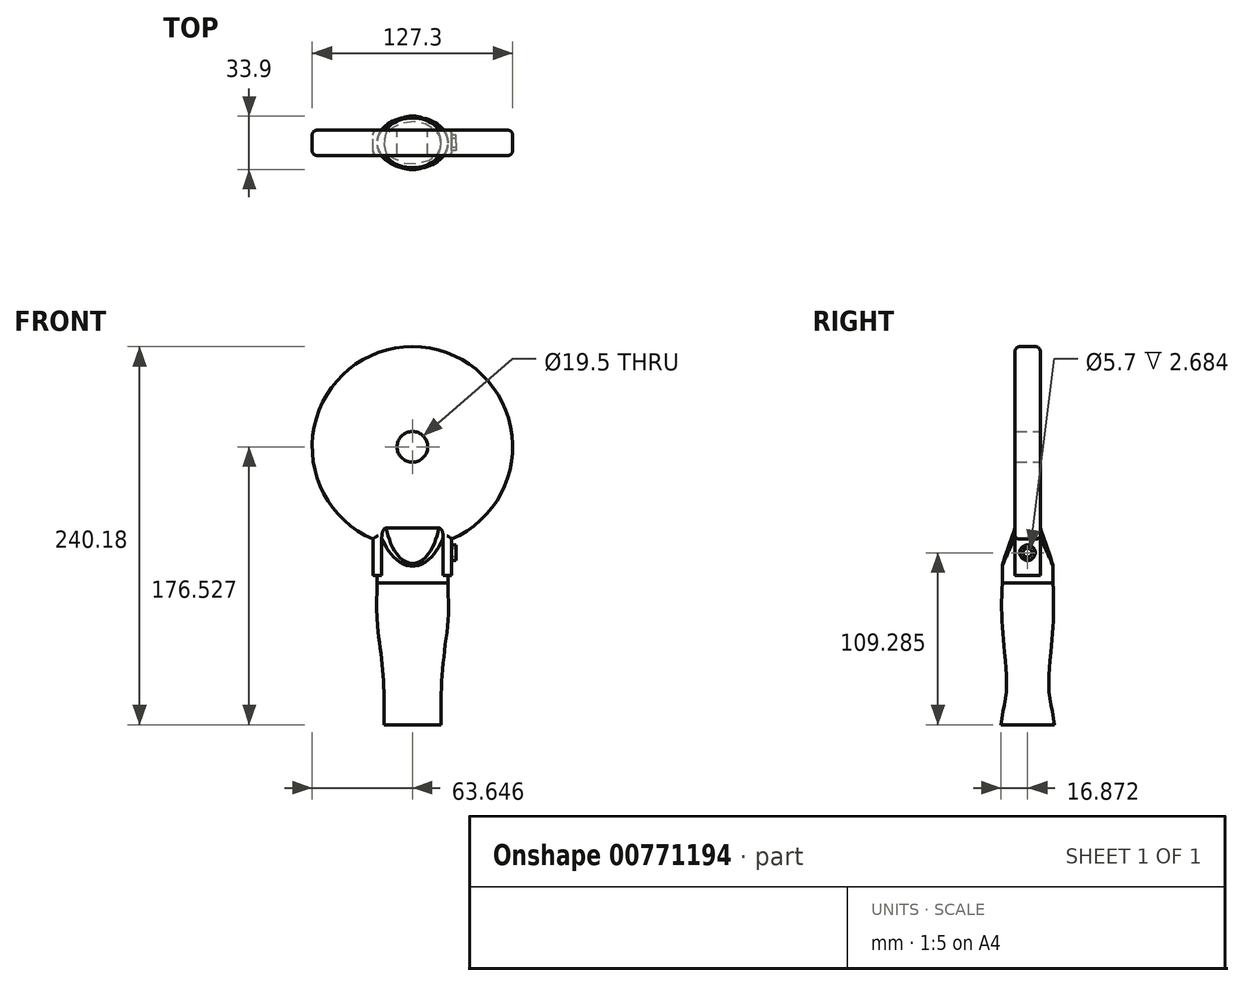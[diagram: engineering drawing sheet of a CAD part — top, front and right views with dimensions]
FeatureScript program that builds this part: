
annotation { "Feature Type Name" : "Feature", "Feature Type Description" : "" }
export const myFeature = defineFeature(function(context is Context, id is Id, definition is map)
    precondition{}
    {
        {
            var Q0;
            Q0=qCreatedBy(makeId("Front.planeOp"),FACE);
            var sketch = newSketch(context, id + "F0", { "sketchPlane" : qUnion([Q0])});
            skLineSegment(sketch, "E0", {"start": v(0, 0) * mm, "end": v(0, 140.42) * mm, "construction": true});
            skSolve(sketch);
        }
        {
            var Q0;
            Q0=qCreatedBy(makeId("Top.planeOp"),FACE);
            var sketch = newSketch(context, id + "F1", { "sketchPlane" : qUnion([Q0])});
            skEllipse(sketch, "E1", {"center": v(0, 0) * mm, "majorRadius": 18.1 * mm, "minorRadius": 16.95 * mm, "majorAxis": v(1, 0)});
            skSolve(sketch);
        }
        {
            var Q0;
            Q0=qCreatedBy(makeId("Top.planeOp"),FACE);
            cPlane(context, id + "F2", {"entities" : qUnion([Q0]), "cplaneType" : CPlaneType.OFFSET, "offset" : 10 * mm, "width" : 150 * mm, "height" : 150 * mm});
        }
        {
            var Q0;
            Q0=qCreatedBy(id+"F2.planeOp",FACE);
            var sketch = newSketch(context, id + "F3", { "sketchPlane" : qUnion([Q0])});
            skEllipse(sketch, "E2", {"center": v(0, 0) * mm, "majorRadius": 18.05 * mm, "minorRadius": 15.3 * mm, "majorAxis": v(1, 0)});
            skSolve(sketch);
        }
        {
            var Q0;
            Q0=qCreatedBy(id+"F2.planeOp",FACE);
            cPlane(context, id + "F4", {"entities" : qUnion([Q0]), "cplaneType" : CPlaneType.OFFSET, "offset" : 10 * mm, "width" : 150 * mm, "height" : 150 * mm});
        }
        {
            var Q0;
            Q0=qCreatedBy(id+"F4.planeOp",FACE);
            var sketch = newSketch(context, id + "F5", { "sketchPlane" : qUnion([Q0])});
            skEllipse(sketch, "E3", {"center": v(0, 0) * mm, "majorRadius": 18.2 * mm, "minorRadius": 13.6 * mm, "majorAxis": v(1, 0)});
            skSolve(sketch);
        }
        {
            var Q0;
            Q0=qCreatedBy(id+"F4.planeOp",FACE);
            cPlane(context, id + "F6", {"entities" : qUnion([Q0]), "cplaneType" : CPlaneType.OFFSET, "offset" : 10 * mm, "width" : 150 * mm, "height" : 150 * mm});
        }
        {
            var Q0;
            Q0=qCreatedBy(id+"F6.planeOp",FACE);
            var sketch = newSketch(context, id + "F7", { "sketchPlane" : qUnion([Q0])});
            skEllipse(sketch, "E4", {"center": v(0, 0) * mm, "majorRadius": 18.55 * mm, "minorRadius": 13.55 * mm, "majorAxis": v(1, 0)});
            skSolve(sketch);
        }
        {
            var Q0;
            Q0=qCreatedBy(id+"F6.planeOp",FACE);
            cPlane(context, id + "F8", {"entities" : qUnion([Q0]), "cplaneType" : CPlaneType.OFFSET, "offset" : 10 * mm, "width" : 150 * mm, "height" : 150 * mm});
        }
        {
            var Q0;
            Q0=qCreatedBy(id+"F8.planeOp",FACE);
            var sketch = newSketch(context, id + "F9", { "sketchPlane" : qUnion([Q0])});
            skEllipse(sketch, "E5", {"center": v(0, 0) * mm, "majorRadius": 19.5 * mm, "minorRadius": 14.15 * mm, "majorAxis": v(1, 0)});
            skSolve(sketch);
        }
        {
            var Q0;
            Q0=qCreatedBy(id+"F8.planeOp",FACE);
            cPlane(context, id + "F10", {"entities" : qUnion([Q0]), "cplaneType" : CPlaneType.OFFSET, "offset" : 10 * mm, "width" : 150 * mm, "height" : 150 * mm});
        }
        {
            var Q0;
            Q0=qCreatedBy(id+"F10.planeOp",FACE);
            var sketch = newSketch(context, id + "F11", { "sketchPlane" : qUnion([Q0])});
            skEllipse(sketch, "E6", {"center": v(0, 0) * mm, "majorRadius": 20.7 * mm, "minorRadius": 15.05 * mm, "majorAxis": v(1, 0)});
            skSolve(sketch);
        }
        {
            var Q0;
            Q0=qCreatedBy(id+"F10.planeOp",FACE);
            cPlane(context, id + "F12", {"entities" : qUnion([Q0]), "cplaneType" : CPlaneType.OFFSET, "offset" : 10 * mm, "width" : 150 * mm, "height" : 150 * mm});
        }
        {
            var Q0;
            Q0=qCreatedBy(id+"F12.planeOp",FACE);
            var sketch = newSketch(context, id + "F13", { "sketchPlane" : qUnion([Q0])});
            skEllipse(sketch, "E7", {"center": v(0, 0) * mm, "majorRadius": 22 * mm, "minorRadius": 15.9 * mm, "majorAxis": v(1, 0)});
            skSolve(sketch);
        }
        {
            var Q0;
            Q0=qCreatedBy(id+"F12.planeOp",FACE);
            cPlane(context, id + "F14", {"entities" : qUnion([Q0]), "cplaneType" : CPlaneType.OFFSET, "offset" : 10 * mm, "width" : 150 * mm, "height" : 150 * mm});
        }
        {
            var Q0;
            Q0=qCreatedBy(id+"F14.planeOp",FACE);
            var sketch = newSketch(context, id + "F15", { "sketchPlane" : qUnion([Q0])});
            skEllipse(sketch, "E8", {"center": v(0, 0) * mm, "majorRadius": 22.7 * mm, "minorRadius": 16.4 * mm, "majorAxis": v(1, 0)});
            skSolve(sketch);
        }
        {
            var Q0;
            Q0=qCreatedBy(id+"F14.planeOp",FACE);
            cPlane(context, id + "F16", {"entities" : qUnion([Q0]), "cplaneType" : CPlaneType.OFFSET, "offset" : 10 * mm, "width" : 150 * mm, "height" : 150 * mm});
        }
        {
            var Q0;
            Q0=qCreatedBy(id+"F16.planeOp",FACE);
            var sketch = newSketch(context, id + "F17", { "sketchPlane" : qUnion([Q0])});
            skEllipse(sketch, "E9", {"center": v(0, 0) * mm, "majorRadius": 22.7 * mm, "minorRadius": 16.5 * mm, "majorAxis": v(1, 0)});
            skSolve(sketch);
        }
        {
            var Q0;
            Q0=qCreatedBy(id+"F16.planeOp",FACE);
            cPlane(context, id + "F18", {"entities" : qUnion([Q0]), "cplaneType" : CPlaneType.OFFSET, "offset" : 10 * mm, "width" : 150 * mm, "height" : 150 * mm});
        }
        {
            var Q0;
            Q0=qCreatedBy(id+"F18.planeOp",FACE);
            var sketch = newSketch(context, id + "F19", { "sketchPlane" : qUnion([Q0])});
            skEllipse(sketch, "E10", {"center": v(0, 0) * mm, "majorRadius": 22.5 * mm, "minorRadius": 16.1 * mm, "majorAxis": v(1, 0)});
            skSolve(sketch);
        }
        {
            var Q0;
            Q0=makeQuery(id+"F1.imprint","IMPRINT",FACE,{"disambiguationData":[TD([[makeQuery(id+"F1.imprint","IMPRINT",EDGE,{"derivedFrom":sQuery(id+"F1.wireOp",EDGE,"E1")}),1.0]])]});
            var Q1;
            Q1=makeQuery(id+"F3.imprint","IMPRINT",FACE,{"disambiguationData":[TD([[makeQuery(id+"F3.imprint","IMPRINT",EDGE,{"derivedFrom":sQuery(id+"F3.wireOp",EDGE,"E2")}),1.0]])]});
            var Q2;
            Q2=makeQuery(id+"F5.imprint","IMPRINT",FACE,{"disambiguationData":[TD([[makeQuery(id+"F5.imprint","IMPRINT",EDGE,{"derivedFrom":sQuery(id+"F5.wireOp",EDGE,"E3")}),1.0]])]});
            var Q3;
            Q3=makeQuery(id+"F7.imprint","IMPRINT",FACE,{"disambiguationData":[TD([[makeQuery(id+"F7.imprint","IMPRINT",EDGE,{"derivedFrom":sQuery(id+"F7.wireOp",EDGE,"E4")}),1.0]])]});
            var Q4;
            Q4=makeQuery(id+"F9.imprint","IMPRINT",FACE,{"disambiguationData":[TD([[makeQuery(id+"F9.imprint","IMPRINT",EDGE,{"derivedFrom":sQuery(id+"F9.wireOp",EDGE,"E5")}),1.0]])]});
            var Q5;
            Q5=makeQuery(id+"F11.imprint","IMPRINT",FACE,{"disambiguationData":[TD([[makeQuery(id+"F11.imprint","IMPRINT",EDGE,{"derivedFrom":sQuery(id+"F11.wireOp",EDGE,"E6")}),1.0]])]});
            var Q6;
            Q6=makeQuery(id+"F13.imprint","IMPRINT",FACE,{"disambiguationData":[TD([[makeQuery(id+"F13.imprint","IMPRINT",EDGE,{"derivedFrom":sQuery(id+"F13.wireOp",EDGE,"E7")}),1.0]])]});
            var Q7;
            Q7=makeQuery(id+"F15.imprint","IMPRINT",FACE,{"disambiguationData":[TD([[makeQuery(id+"F15.imprint","IMPRINT",EDGE,{"derivedFrom":sQuery(id+"F15.wireOp",EDGE,"E8")}),1.0]])]});
            var Q8;
            Q8=makeQuery(id+"F17.imprint","IMPRINT",FACE,{"disambiguationData":[TD([[makeQuery(id+"F17.imprint","IMPRINT",EDGE,{"derivedFrom":sQuery(id+"F17.wireOp",EDGE,"E9")}),1.0]])]});
            var Q9;
            Q9=makeQuery(id+"F19.imprint","IMPRINT",FACE,{"disambiguationData":[TD([[makeQuery(id+"F19.imprint","IMPRINT",EDGE,{"derivedFrom":sQuery(id+"F19.wireOp",EDGE,"E10")}),1.0]])]});
            loft(context, id + "F20", {"sheetProfilesArray" : [{ "sheetProfileEntities" : qUnion([Q0]) }, { "sheetProfileEntities" : qUnion([Q1]) }, { "sheetProfileEntities" : qUnion([Q2]) }, { "sheetProfileEntities" : qUnion([Q3]) }, { "sheetProfileEntities" : qUnion([Q4]) }, { "sheetProfileEntities" : qUnion([Q5]) }, { "sheetProfileEntities" : qUnion([Q6]) }, { "sheetProfileEntities" : qUnion([Q7]) }, { "sheetProfileEntities" : qUnion([Q8]) }, { "sheetProfileEntities" : qUnion([Q9]) }]});
        }
        {
            var Q0;
            Q0=makeQuery(id+"F20.opLoft","CAP_FACE",FACE,{"disambiguationData":[OSD([makeQuery(id+"F19.imprint","IMPRINT",FACE,{"disambiguationData":[TD([[makeQuery(id+"F19.imprint","IMPRINT",EDGE,{"derivedFrom":sQuery(id+"F19.wireOp",EDGE,"E10")}),1.0]])]})])],"isStart":true});
            extrude(context, id + "F21", {"entities" : qUnion([Q0]), "operationType" : NewBodyOperationType.ADD, "depth" : 35 * mm, "offsetDistance" : 25 * mm});
        }
        {
            var Q0;
            Q0=qCreatedBy(makeId("Front.planeOp"),FACE);
            var sketch = newSketch(context, id + "F22", { "sketchPlane" : qUnion([Q0])});
            skLineSegment(sketch, "E11.top", {"start": v(-0.08, 119.9) * mm, "end": v(24.82, 119.9) * mm});
            skLineSegment(sketch, "E11.left", {"start": v(-0.08, 89.9) * mm, "end": v(-0.08, 119.9) * mm});
            skLineSegment(sketch, "E12.MirrorCS", {"start": v(-0.08, 119.9) * mm, "end": v(-24.98, 119.9) * mm});
            skLineSegment(sketch, "E13", {"start": v(-0.08, 89.38) * mm, "end": v(-0.08, 240.38) * mm, "construction": true});
            skCircle(sketch, "E14", {"center": v(-0.08, 176.53) * mm, "radius": 9.75 * mm});
            skCircle(sketch, "E15", {"center": v(-0.08, 176.53) * mm, "radius": 63.65 * mm});
            skLineSegment(sketch, "E16", {"start": v(-0.08, 119.9) * mm, "end": v(54.23, 119.9) * mm, "construction": true});
            skLineSegment(sketch, "E17", {"start": v(-0.08, 89.9) * mm, "end": v(-0.08, 94.9) * mm});
            skLineSegment(sketch, "E18", {"start": v(-0.08, 94.9) * mm, "end": v(24.82, 94.9) * mm});
            skLineSegment(sketch, "E19.MirrorCS", {"start": v(-0.08, 100.44) * mm, "end": v(-0.08, -50.56) * mm, "construction": true});
            skLineSegment(sketch, "E20", {"start": v(-0.08, 94.9) * mm, "end": v(-24.98, 94.9) * mm});
            skLineSegment(sketch, "E21", {"start": v(-24.98, 94.9) * mm, "end": v(-24.98, 119.9) * mm});
            skLineSegment(sketch, "E22", {"start": v(24.82, 94.9) * mm, "end": v(24.82, 119.9) * mm});
            skSolve(sketch);
        }
        {
            var Q0;
            Q0=qCreatedBy(makeId("Right.planeOp"),FACE);
            var sketch = newSketch(context, id + "F23", { "sketchPlane" : qUnion([Q0])});
            skLineSegment(sketch, "E23", {"start": v(-0.08, 0.28) * mm, "end": v(-0.08, 109.28) * mm});
            skCircle(sketch, "E24", {"center": v(-0.08, 109.28) * mm, "radius": 4.9 * mm});
            skCircle(sketch, "E25", {"center": v(-0.08, 109.28) * mm, "radius": 2.85 * mm});
            skSolve(sketch);
        }
        {
            var Q0;
            Q0 = qSketchRegion(id + "F23", true);
            extrude(context, id + "F24", {"entities" : qUnion([Q0]), "operationType" : NewBodyOperationType.ADD, "depth" : 27.5 * mm, "offsetDistance" : 25 * mm});
        }
        {
            var Q0;
            {var subQ5=sQuery(id+"F22.wireOp",EDGE,"E11.top");Q0=makeQuery(id+"F22.imprint","IMPRINT",FACE,{"disambiguationData":[TD([[makeQuery(id+"F22.imprint","IMPRINT",EDGE,{"derivedFrom":subQ5}),1.0]])]});}
            var Q1;
            {var subQ0=sQuery(id+"F22.wireOp",EDGE,"E11.bottom");Q1=makeQuery(id+"F22.imprint","IMPRINT",FACE,{"disambiguationData":[TD([[makeQuery(id+"F22.imprint","IMPRINT",EDGE,{"derivedFrom":subQ0}),1.0]])]});}
            var Q2;
            {var subQ0=sQuery(id+"F22.wireOp",EDGE,"E11.top");Q2=makeQuery(id+"F22.imprint","IMPRINT",FACE,{"disambiguationData":[TD([[makeQuery(id+"F22.imprint","IMPRINT",EDGE,{"derivedFrom":subQ0}),-1.0]])]});}
            var Q3;
            {var subQ0=sQuery(id+"F22.wireOp",EDGE,"E12.MirrorCS");Q3=makeQuery(id+"F22.imprint","IMPRINT",FACE,{"disambiguationData":[TD([[makeQuery(id+"F22.imprint","IMPRINT",EDGE,{"derivedFrom":subQ0}),1.0]])]});}
            var Q4;
            {var subQ0=sQuery(id+"F22.wireOp",EDGE,"55a6d1cb-0f40-4dd8-971e-41e56460f39b0.MirrorCS");Q4=makeQuery(id+"F22.imprint","IMPRINT",FACE,{"disambiguationData":[TD([[makeQuery(id+"F22.imprint","IMPRINT",EDGE,{"derivedFrom":subQ0}),-1.0]])]});}
            extrude(context, id + "F25", {"entities" : qUnion([Q0, Q1, Q2, Q3, Q4]), "operationType" : NewBodyOperationType.ADD, "endBound" : BoundingType.SYMMETRIC, "depth" : 16 * mm, "offsetDistance" : 25 * mm});
        }
        {
            var Q0;
            {var subQ0=sQuery(id+"F22.wireOp",EDGE,"E18");Q0=makeQuery(id+"F22.imprint","IMPRINT",FACE,{"disambiguationData":[TD([[makeQuery(id+"F22.imprint","IMPRINT",EDGE,{"derivedFrom":subQ0}),1.0]])]});}
            extrude(context, id + "F26", {"entities" : qUnion([Q0]), "operationType" : NewBodyOperationType.ADD, "endBound" : BoundingType.SYMMETRIC, "depth" : 16 * mm, "offsetDistance" : 25 * mm});
        }
        {
            var Q0;
            {var subQ0=sQuery(id+"F22.wireOp",EDGE,"E20");Q0=makeQuery(id+"F22.imprint","IMPRINT",FACE,{"disambiguationData":[TD([[makeQuery(id+"F22.imprint","IMPRINT",EDGE,{"derivedFrom":subQ0}),-1.0]])]});}
            extrude(context, id + "F27", {"entities" : qUnion([Q0]), "operationType" : NewBodyOperationType.ADD, "endBound" : BoundingType.SYMMETRIC, "depth" : 16 * mm, "offsetDistance" : 25 * mm});
        }
        {
            var Q0;
            Q0=qCreatedBy(makeId("Right.planeOp"),FACE);
            var sketch = newSketch(context, id + "F28", { "sketchPlane" : qUnion([Q0])});
            skLineSegment(sketch, "E26", {"start": v(-20.12, 90) * mm, "end": v(-8, 125) * mm});
            skLineSegment(sketch, "E27", {"start": v(-8, 125) * mm, "end": v(-20.74, 137.98) * mm});
            skLineSegment(sketch, "E28", {"start": v(-20.74, 137.98) * mm, "end": v(-20.12, 90) * mm});
            skLineSegment(sketch, "E29.MirrorCS", {"start": v(8, 125) * mm, "end": v(20.74, 137.98) * mm});
            skLineSegment(sketch, "E30.MirrorCS", {"start": v(20.12, 90) * mm, "end": v(8, 125) * mm});
            skLineSegment(sketch, "E31.MirrorCS", {"start": v(20.74, 137.98) * mm, "end": v(20.12, 90) * mm});
            skSolve(sketch);
        }
        {
            var Q0;
            Q0=makeQuery(id+"F28.imprint","IMPRINT",FACE,{"disambiguationData":[TD([[makeQuery(id+"F28.imprint","IMPRINT",EDGE,{"derivedFrom":sQuery(id+"F28.wireOp",EDGE,"E26")}),1.0]])]});
            var Q1;
            Q1=makeQuery(id+"F28.imprint","IMPRINT",FACE,{"disambiguationData":[TD([[makeQuery(id+"F28.imprint","IMPRINT",EDGE,{"derivedFrom":sQuery(id+"F28.wireOp",EDGE,"E29.MirrorCS")}),-1.0]])]});
            extrude(context, id + "F29", {"entities" : qUnion([Q0, Q1]), "operationType" : NewBodyOperationType.REMOVE, "endBound" : BoundingType.SYMMETRIC, "oppositeDirection" : true, "depth" : 70 * mm, "offsetDistance" : 25 * mm});
        }
        {
            var Q0;
            Q0=makeQuery(id+"F25.opExtrude","CAP_EDGE",EDGE,{"disambiguationData":[OSD([sQuery(id+"F22.wireOp",EDGE,"d095e0c7-c276-491f-b3f2-35c4f7110da40.MirrorCS")])],"isStart":true});
            var Q1;
            Q1=makeQuery(id+"F25.opExtrude","CAP_EDGE",EDGE,{"disambiguationData":[OSD([sQuery(id+"F22.wireOp",EDGE,"E15")])],"isStart":true});
            var Q2;
            Q2=makeQuery(id+"F25.opExtrude","CAP_EDGE",EDGE,{"disambiguationData":[OSD([sQuery(id+"F22.wireOp",EDGE,"E15")])],"isStart":false});
            var Q3;
            Q3=makeQuery(id+"F25.opExtrude","CAP_EDGE",EDGE,{"disambiguationData":[OSD([sQuery(id+"F22.wireOp",EDGE,"d095e0c7-c276-491f-b3f2-35c4f7110da40.MirrorCS")])],"isStart":false});
            var Q4;
            Q4=makeQuery(id+"F25.opExtrude","CAP_EDGE",EDGE,{"disambiguationData":[OSD([sQuery(id+"F22.wireOp",EDGE,"E11.right")])],"isStart":true});
            var Q5;
            Q5=makeQuery(id+"F25.opExtrude","CAP_EDGE",EDGE,{"disambiguationData":[OSD([sQuery(id+"F22.wireOp",EDGE,"E11.right")])],"isStart":false});
            fillet(context, id + "F30", {"entities" : qUnion([Q0, Q1, Q2, Q3, Q4, Q5]), "radius" : 3 * mm, "tangentPropagation" : true, "allowEdgeOverflow" : false});
        }
        {
            var Q0;
            {var subQ0=sQuery(id+"F19.wireOp",EDGE,"E10");Q0=makeQuery(id+"F29.boolean.opBoolean","INTERSECT",EDGE,{"derivedFrom":[makeQuery(id+"F25.boolean.opBoolean","SPLIT",FACE,{"disambiguationData":[TD([makeQuery(id+"F25.opExtrude","CAP_FACE",FACE,{"disambiguationData":[OSD([sQuery(id+"F22.wireOp",EDGE,"E11.bottom"),sQuery(id+"F22.wireOp",EDGE,"E11.right"),sQuery(id+"F22.wireOp",EDGE,"d095e0c7-c276-491f-b3f2-35c4f7110da40.MirrorCS"),sQuery(id+"F22.wireOp",EDGE,"55a6d1cb-0f40-4dd8-971e-41e56460f39b0.MirrorCS"),sQuery(id+"F22.wireOp",EDGE,"E14"),sQuery(id+"F22.wireOp",EDGE,"E15")])],"isStart":false})])],"derivedFrom":makeQuery(id+"F21.opExtrude","SWEPT_FACE",FACE,{"disambiguationData":[OSD([subQ0])]})}),makeQuery(id+"F29.opExtrude","SWEPT_FACE",FACE,{"disambiguationData":[OSD([sQuery(id+"F28.wireOp",EDGE,"E26")])]})]});}
            var Q1;
            {var subQ0=sQuery(id+"F19.wireOp",EDGE,"E10");Q1=makeQuery(id+"F29.boolean.opBoolean","INTERSECT",EDGE,{"derivedFrom":[makeQuery(id+"F25.boolean.opBoolean","SPLIT",FACE,{"disambiguationData":[TD([makeQuery(id+"F25.opExtrude","CAP_FACE",FACE,{"disambiguationData":[OSD([sQuery(id+"F22.wireOp",EDGE,"E11.bottom"),sQuery(id+"F22.wireOp",EDGE,"E11.right"),sQuery(id+"F22.wireOp",EDGE,"d095e0c7-c276-491f-b3f2-35c4f7110da40.MirrorCS"),sQuery(id+"F22.wireOp",EDGE,"55a6d1cb-0f40-4dd8-971e-41e56460f39b0.MirrorCS"),sQuery(id+"F22.wireOp",EDGE,"E14"),sQuery(id+"F22.wireOp",EDGE,"E15")])],"isStart":true})])],"derivedFrom":makeQuery(id+"F21.opExtrude","SWEPT_FACE",FACE,{"disambiguationData":[OSD([subQ0])]})}),makeQuery(id+"F29.opExtrude","SWEPT_FACE",FACE,{"disambiguationData":[OSD([sQuery(id+"F28.wireOp",EDGE,"E30.MirrorCS")])]})]});}
            fillet(context, id + "F31", {"entities" : qUnion([Q0, Q1]), "radius" : 5 * mm, "tangentPropagation" : true, "allowEdgeOverflow" : false});
        }
        {
            var Q0;
            Q0=makeQuery(id+"F27.opExtrude","CAP_EDGE",EDGE,{"disambiguationData":[OSD([sQuery(id+"F22.wireOp",EDGE,"E21")])],"isStart":true});
            var Q1;
            Q1=makeQuery(id+"F27.opExtrude","CAP_EDGE",EDGE,{"disambiguationData":[OSD([sQuery(id+"F22.wireOp",EDGE,"E21")])],"isStart":false});
            fillet(context, id + "F32", {"entities" : qUnion([Q0, Q1]), "radius" : 3 * mm, "tangentPropagation" : true, "rho" : 0.5, "crossSection" : FilletCrossSection.CONIC, "allowEdgeOverflow" : false});
        }
        {
            var Q0;
            Q0=makeQuery(id+"F26.opExtrude","CAP_EDGE",EDGE,{"disambiguationData":[OSD([sQuery(id+"F22.wireOp",EDGE,"E22")])],"isStart":false});
            var Q1;
            Q1=makeQuery(id+"F26.opExtrude","CAP_EDGE",EDGE,{"disambiguationData":[OSD([sQuery(id+"F22.wireOp",EDGE,"E22")])],"isStart":true});
            fillet(context, id + "F33", {"entities" : qUnion([Q0, Q1]), "radius" : 3 * mm, "tangentPropagation" : true, "rho" : 0.5, "crossSection" : FilletCrossSection.CONIC, "allowEdgeOverflow" : false});
        }
    });
